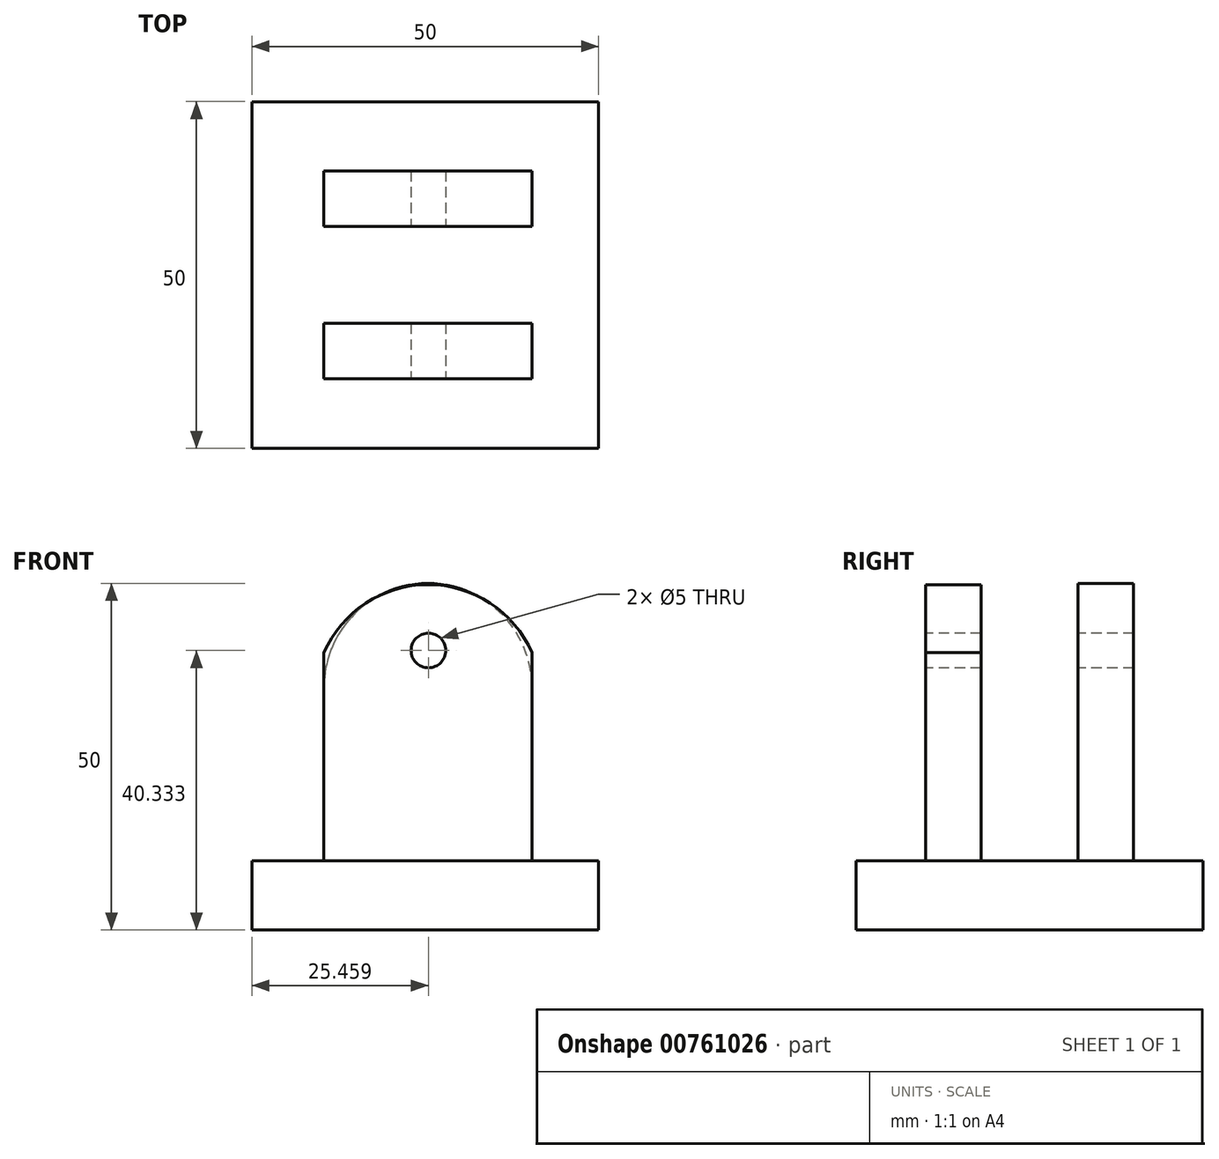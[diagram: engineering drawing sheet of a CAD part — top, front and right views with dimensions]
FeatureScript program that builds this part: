
annotation { "Feature Type Name" : "Feature", "Feature Type Description" : "" }
export const myFeature = defineFeature(function(context is Context, id is Id, definition is map)
    precondition{}
    {
        {
            var Q0;
            Q0=qCreatedBy(makeId("Top.planeOp"),FACE);
            var sketch = newSketch(context, id + "F0", { "sketchPlane" : qUnion([Q0])});
            skLineSegment(sketch, "E0.bottom", {"start": v(-23.83, 21.89) * mm, "end": v(26.17, 21.89) * mm});
            skLineSegment(sketch, "E0.top", {"start": v(-23.83, -28.11) * mm, "end": v(26.17, -28.11) * mm});
            skLineSegment(sketch, "E0.left", {"start": v(-23.83, 21.89) * mm, "end": v(-23.83, -28.11) * mm});
            skLineSegment(sketch, "E0.right", {"start": v(26.17, 21.89) * mm, "end": v(26.17, -28.11) * mm});
            skSolve(sketch);
        }
        {
            var Q0;
            Q0 = qSketchRegion(id + "F0", true);
            extrude(context, id + "F1", {"entities" : qUnion([Q0]), "depth" : 10 * mm, "offsetDistance" : 25 * mm});
        }
        {
            var Q0;
            Q0=makeQuery(id+"F1.opExtrude","CAP_FACE",FACE,{"disambiguationData":[OSD([sQuery(id+"F0.wireOp",EDGE,"E0.bottom"),sQuery(id+"F0.wireOp",EDGE,"E0.top"),sQuery(id+"F0.wireOp",EDGE,"E0.left"),sQuery(id+"F0.wireOp",EDGE,"E0.right")])],"isStart":false});
            var sketch = newSketch(context, id + "F2", { "sketchPlane" : qUnion([Q0])});
            skLineSegment(sketch, "E1.bottom", {"start": v(-13.44, 11.89) * mm, "end": v(16.56, 11.89) * mm});
            skLineSegment(sketch, "E1.top", {"start": v(-13.44, 3.89) * mm, "end": v(16.56, 3.89) * mm});
            skLineSegment(sketch, "E1.left", {"start": v(-13.44, 11.89) * mm, "end": v(-13.44, 3.89) * mm});
            skLineSegment(sketch, "E1.right", {"start": v(16.56, 11.89) * mm, "end": v(16.56, 3.89) * mm});
            skSolve(sketch);
        }
        {
            var Q0;
            Q0=makeQuery(id+"F2.imprint","IMPRINT",FACE,{"disambiguationData":[TD([[makeQuery(id+"F2.imprint","IMPRINT",EDGE,{"derivedFrom":sQuery(id+"F2.wireOp",EDGE,"E1.bottom")}),-1.0]])]});
            extrude(context, id + "F3", {"entities" : qUnion([Q0]), "operationType" : NewBodyOperationType.ADD, "depth" : 40 * mm, "offsetDistance" : 25 * mm});
        }
        {
            var Q0;
            Q0=makeQuery(id+"F1.opExtrude","CAP_FACE",FACE,{"disambiguationData":[OSD([sQuery(id+"F0.wireOp",EDGE,"E0.bottom"),sQuery(id+"F0.wireOp",EDGE,"E0.top"),sQuery(id+"F0.wireOp",EDGE,"E0.left"),sQuery(id+"F0.wireOp",EDGE,"E0.right")])],"isStart":false});
            var sketch = newSketch(context, id + "F4", { "sketchPlane" : qUnion([Q0])});
            skLineSegment(sketch, "E2.bottom", {"start": v(-13.44, -10.11) * mm, "end": v(16.56, -10.11) * mm});
            skLineSegment(sketch, "E2.top", {"start": v(-13.44, -18.11) * mm, "end": v(16.56, -18.11) * mm});
            skLineSegment(sketch, "E2.left", {"start": v(-13.44, -10.11) * mm, "end": v(-13.44, -18.11) * mm});
            skLineSegment(sketch, "E2.right", {"start": v(16.56, -10.11) * mm, "end": v(16.56, -18.11) * mm});
            skSolve(sketch);
        }
        {
            var Q0;
            Q0=makeQuery(id+"F4.imprint","IMPRINT",FACE,{"disambiguationData":[TD([[makeQuery(id+"F4.imprint","IMPRINT",EDGE,{"derivedFrom":sQuery(id+"F4.wireOp",EDGE,"E2.bottom")}),-1.0]])]});
            extrude(context, id + "F5", {"entities" : qUnion([Q0]), "operationType" : NewBodyOperationType.ADD, "depth" : 30 * mm, "offsetDistance" : 25 * mm});
        }
        {
            var Q0;
            Q0=makeQuery(id+"F5.opExtrude","SWEPT_FACE",FACE,{"disambiguationData":[OSD([sQuery(id+"F4.wireOp",EDGE,"E2.top")])]});
            var sketch = newSketch(context, id + "F6", { "sketchPlane" : qUnion([Q0])});
            skArc(sketch, "E3", {"start": v(16.56, 40) * mm, "mid": v(1.56, 49.83) * mm, "end": v(-13.44, 40) * mm});
            skSolve(sketch);
        }
        {
            var Q0;
            Q0=makeQuery(id+"F6.imprint","IMPRINT",FACE,{"disambiguationData":[TD([[makeQuery(id+"F6.imprint","IMPRINT",EDGE,{"derivedFrom":sQuery(id+"F6.wireOp",EDGE,"E3")}),1.0]])]});
            extrude(context, id + "F7", {"entities" : qUnion([Q0]), "operationType" : NewBodyOperationType.ADD, "oppositeDirection" : true, "depth" : 8 * mm, "offsetDistance" : 25 * mm});
        }
        {
            var Q0;
            {var subQ0=sQuery(id+"F4.wireOp",EDGE,"E2.top");Q0=makeQuery(id+"F7.boolean.opBoolean","MERGE",FACE,{"derivedFrom":[makeQuery(id+"F5.opExtrude","SWEPT_FACE",FACE,{"disambiguationData":[OSD([subQ0])]}),makeQuery(id+"F7.opExtrude","CAP_FACE",FACE,{"disambiguationData":[OSD([subQ0,sQuery(id+"F6.wireOp",EDGE,"E3")])],"isStart":true})]});}
            var sketch = newSketch(context, id + "F8", { "sketchPlane" : qUnion([Q0])});
            skCircle(sketch, "E4", {"center": v(1.56, 40.9) * mm, "radius": 2.5 * mm});
            skPoint(sketch, "E4.centerSnap0", {"position": v(1.56, 49.83) * mm});
            skSolve(sketch);
        }
        {
            var Q0;
            Q0=makeQuery(id+"F3.opExtrude","CAP_EDGE",EDGE,{"disambiguationData":[OSD([sQuery(id+"F2.wireOp",EDGE,"E1.right")])],"isStart":false});
            var Q1;
            Q1=makeQuery(id+"F3.opExtrude","CAP_EDGE",EDGE,{"disambiguationData":[OSD([sQuery(id+"F2.wireOp",EDGE,"E1.left")])],"isStart":false});
            fillet(context, id + "F9", {"entities" : qUnion([Q0, Q1]), "radius" : 15 * mm, "tangentPropagation" : true, "allowEdgeOverflow" : false});
        }
        {
            var Q0;
            Q0=makeQuery(id+"F8.imprint","IMPRINT",FACE,{"disambiguationData":[TD([[makeQuery(id+"F8.imprint","IMPRINT",EDGE,{"derivedFrom":sQuery(id+"F8.wireOp",EDGE,"E4")}),-1.0]])]});
            var sketch = newSketch(context, id + "F10", { "sketchPlane" : qUnion([Q0])});
            skPoint(sketch, "E5", {"position": v(1.63, 40.33) * mm});
            skSolve(sketch);
        }
        {
            var Q0;
            Q0=sQuery(id+"F10.wireOp",VERTEX,"E5");
            var Q1;
            Q1=makeQuery(id+"F1.opExtrude","SWEPT_BODY",BODY,{"disambiguationData":[OSD([sQuery(id+"F0.wireOp",EDGE,"E0.bottom"),sQuery(id+"F0.wireOp",EDGE,"E0.top"),sQuery(id+"F0.wireOp",EDGE,"E0.left"),sQuery(id+"F0.wireOp",EDGE,"E0.right")])]});
            hole(context, id + "F11", {"style" : HoleStyle.SIMPLE, "endStyle" : HoleEndStyle.THROUGH, "holeDiameter" : 5 * mm, "majorDiameter" : 5 * mm, "isTappedThrough" : true, "tappedDepth" : 12 * mm, "tapClearance" : 3, "locations" : qUnion([Q0]), "scope" : qUnion([Q1])});
        }
    });
